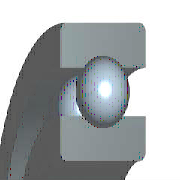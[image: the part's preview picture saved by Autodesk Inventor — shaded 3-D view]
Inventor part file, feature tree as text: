
AUTODESK INVENTOR PART (.ipt)
format: ipt  version: 2015 SP2 (Build 190223200, 223)  size: 345,088 bytes
history: native  units: mm (DEFAULTED — no unit token found)
features: sketch x5, other x3, plane x2, pattern_circular x1, fillet x1
ambient origin geometry x8: Origin, YZ Plane, XZ Plane, XY Plane, X Axis, Y Axis, Z Axis, Center Point
bodies: Solid1 (feature_tree)
feature tree (12):
  sketch  "Sketch1"  dims[d2=72.0mm]
  other  "WorkPoint1"
  other  "WorkAxis1"
  plane  "WorkPlane3"
  plane  "WorkPlane4"
  sketch  "Sketch4"  dims[d5=7.0mm]
  other  "WorkPoint2"
  pattern_circular  "PolarArray1"  Count=2  [1 undecoded]
  fillet  "Fillet1"  Radius=8.0mm
  sketch  "Sketch2"  dims[d3=22.0mm]
  sketch  "Sketch3"  dims[d4=19.0mm]
  sketch  "Sketch5"  dims[d6=360.0deg d7=0.0mm d8=15.6mm d9=4.2mm d10=360.0deg d11=-7.0mm d12=0.0mm d13=0.0mm d14=15.6001mm d15=4.2001mm d16=360.0deg d17=57.571429mm d19=360.0deg d20=0.3mm d21=6.24mm d22=7.5mm d23=8.76mm d26=0.0mm d27=0.0mm d28=0.0mm d29=0.0mm d30=0.0mm]
note: 1 required parameter value undecoded (feature->parameter linkage not recoverable at this tier; creation-order binding heuristic only, values carry confidence <= 0.55)
